FCSTD DOCUMENT  (FreeCAD 1.0R39319 (Git))
Label: Vise Base
License: All rights reserved
LicenseURL: https://en.wikipedia.org/wiki/All_rights_reserved
objects: App::Link×7, App::FeaturePython×7, Assembly::JointGroup×1, Assembly::AssemblyObject×1
EXTERNAL_REF file=Extrusions.FCStd obj=Body
EXTERNAL_REF file=Extrusions.FCStd obj=Body001
EXTERNAL_REF file=Extrusions.FCStd obj=product0

FEATURE [App::Link] _3cm_extrusion  label="23cm extrusion"
  LinkPlacement = pos=(0,0,0) rot=(0.707107,0,0.707107;3.14159rad)
  LinkedObject = -> <external Extrusions.FCStd>#Body
  Placement = pos=(0,0,0) rot=(0.707107,0,0.707107;3.14159rad)
FEATURE [App::FeaturePython] GroundedJoint  # Assembly grounded joint (typed FeaturePython)
  ObjectToGround = -> _3cm_extrusion
  Placement = pos=(0,0,0) rot=(0.707107,0,0.707107;3.14159rad)
FEATURE [App::Link] _0cm_Extrusion  label="10cm Extrusion"
  LinkPlacement = pos=(230,40,0) rot=(1,0,0;1.5708rad)
  LinkedObject = -> <external Extrusions.FCStd>#Body001
  Placement = pos=(230,40,0) rot=(1,0,0;1.5708rad)
FEATURE [App::Link] _0cm_Extrusion001  label="10cm Extrusion001"
  LinkPlacement = pos=(-20,40,0) rot=(1,0,0;1.5708rad)
  LinkedObject = -> <external Extrusions.FCStd>#Body001
  Placement = pos=(-20,40,0) rot=(1,0,0;1.5708rad)
FEATURE [App::FeaturePython] GroundedJoint001  # Assembly grounded joint (typed FeaturePython)
  ObjectToGround = -> _0cm_Extrusion001
  Placement = pos=(-20,40,0) rot=(1,0,0;1.5708rad)
FEATURE [App::FeaturePython] GroundedJoint002  # Assembly grounded joint (typed FeaturePython)
  ObjectToGround = -> _0cm_Extrusion
  Placement = pos=(230,40,0) rot=(1,0,0;1.5708rad)
FEATURE [App::Link] product1508
  LinkPlacement = pos=(1.87894e-05,-41,20) rot=(0,1,0;1.5708rad)
  LinkedObject = -> <external Extrusions.FCStd>#product0
  Placement = pos=(1.87894e-05,-41,20) rot=(0,1,0;1.5708rad)
FEATURE [App::Link] product1509
  LinkPlacement = pos=(229.58,-39.643,-0.108443) rot=(0,1,0;4.71239rad)
  LinkedObject = -> <external Extrusions.FCStd>#product0
  Placement = pos=(229.58,-39.643,-0.108443) rot=(0,1,0;4.71239rad)
FEATURE [App::Link] product1510
  LinkPlacement = pos=(210.053,-0.604493,0.170701) rot=(0.57735,0.57735,0.57735;4.18879rad)
  LinkedObject = -> <external Extrusions.FCStd>#product0
  Placement = pos=(210.053,-0.604493,0.170701) rot=(0.57735,0.57735,0.57735;4.18879rad)
FEATURE [App::Link] product1511
  LinkPlacement = pos=(20,-3.72501e-07,20) rot=(-0.57735,0.57735,0.57735;2.0944rad)
  LinkedObject = -> <external Extrusions.FCStd>#product0
  Placement = pos=(20,-3.72501e-07,20) rot=(-0.57735,0.57735,0.57735;2.0944rad)
FEATURE [App::FeaturePython] GroundedJoint003  # Assembly grounded joint (typed FeaturePython)
  ObjectToGround = -> product1508
  Placement = pos=(1.87894e-05,-41,20) rot=(0,1,0;1.5708rad)
FEATURE [App::FeaturePython] GroundedJoint004  # Assembly grounded joint (typed FeaturePython)
  ObjectToGround = -> product1509
  Placement = pos=(229.58,-39.643,-0.108443) rot=(0,-1,0;1.5708rad)
FEATURE [App::FeaturePython] GroundedJoint005  # Assembly grounded joint (typed FeaturePython)
  ObjectToGround = -> product1510
  Placement = pos=(210.053,-0.604493,0.170701) rot=(0.57735,0.57735,0.57735;4.18879rad)
FEATURE [App::FeaturePython] GroundedJoint006  # Assembly grounded joint (typed FeaturePython)
  ObjectToGround = -> product1511
  Placement = pos=(20,-3.72501e-07,20) rot=(-0.57735,0.57735,0.57735;2.0944rad)
FEATURE [Assembly::JointGroup] Joints
  Group = -> [GroundedJoint,GroundedJoint001,GroundedJoint002,GroundedJoint003,GroundedJoint004,GroundedJoint005,GroundedJoint006]
FEATURE [Assembly::AssemblyObject] Assembly
  Group = -> [Joints,_3cm_extrusion,GroundedJoint,_0cm_Extrusion,_0cm_Extrusion001,GroundedJoint001,GroundedJoint002,product1508,product1509,product1510,product1511,GroundedJoint003,GroundedJoint004,GroundedJoint005,GroundedJoint006]
  Origin = -> Origin
  Type = Assembly
